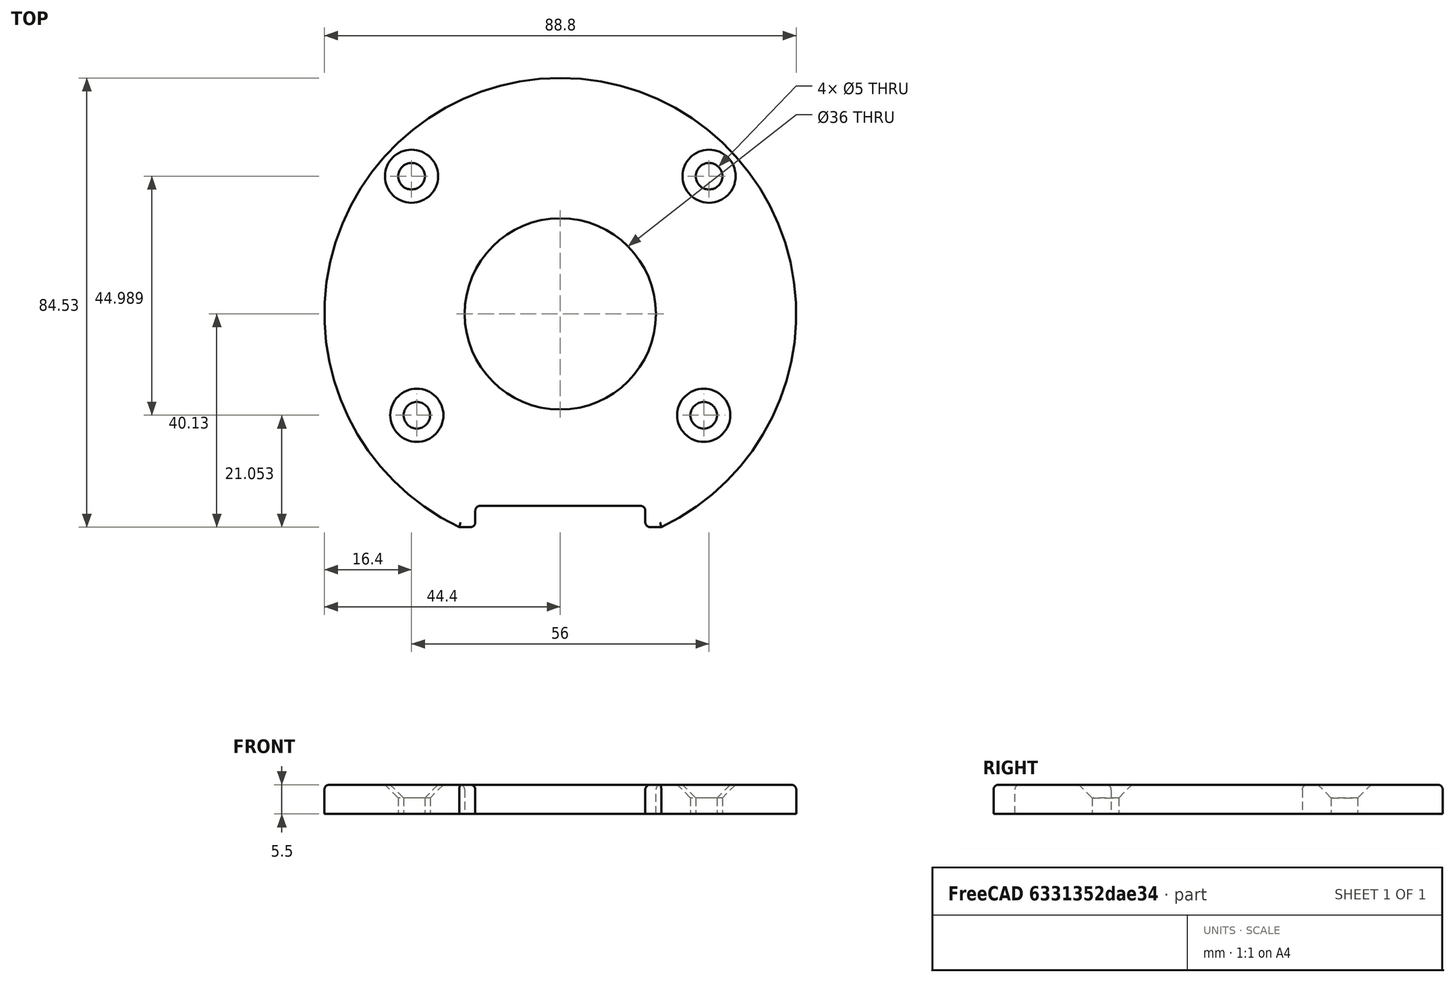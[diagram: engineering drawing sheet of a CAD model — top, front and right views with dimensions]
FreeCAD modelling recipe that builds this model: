
FCSTD DOCUMENT  (FreeCAD 0.19RUnknown)
Label: makita_RT0700CX4-2_base
License: All rights reserved
LicenseURL: http://en.wikipedia.org/wiki/All_rights_reserved
objects: Sketcher::SketchObject×2, PartDesign::Pad×1, PartDesign::Hole×1, PartDesign::Fillet×1, PartDesign::Body×1
note: 9 computed .brp shape members not serialized (recipe doc carries the construction recipe); baked Part::Feature solids carry a one-line shape summary decoded from their .brp

FEATURE [Sketcher::SketchObject] Sketch
  FullyConstrained = true
  MapMode = 5
  Support = -> [XY_Plane]
  sketch-geometry (7):
    g0: ArcOfCircle CenterX=0 CenterY=0 CenterZ=0 NormalX=0 NormalY=0 NormalZ=1 AngleXU=0 Radius=44.4 StartAngle=5.15459 EndAngle=10.5534
    g1: Circle CenterX=0 CenterY=0 CenterZ=0 NormalX=0 NormalY=0 NormalZ=1 AngleXU=0 Radius=18
    g2: LineSegment StartX=-19 StartY=-40.1293 StartZ=0 EndX=-16 EndY=-40.1293 EndZ=0
    g3: LineSegment StartX=-16 StartY=-40.1293 StartZ=0 EndX=-16 EndY=-36.1293 EndZ=0
    g4: LineSegment StartX=-16 StartY=-36.1293 StartZ=0 EndX=16 EndY=-36.1293 EndZ=0
    g5: LineSegment StartX=16 StartY=-36.1293 StartZ=0 EndX=16 EndY=-40.1293 EndZ=0
    g6: LineSegment StartX=16 StartY=-40.1293 StartZ=0 EndX=19 EndY=-40.1293 EndZ=0
  constraints (19):
    c: Coincident(g0,g-1)
    c: Diameter(g0) = 88.8
    c: Coincident(g1,g0)
    c: Diameter(g1) = 36
    c: Horizontal(g2)
    c: DistanceX(g2,g6) = 38
    c: Coincident(g0,g6)
    c: Coincident(g0,g2)
    c: Vertical(g3)
    c: Horizontal(g4)
    c: Vertical(g5)
    c: Coincident(g2,g3)
    c: Coincident(g6,g5)
    c: Tangent(g2,g6)
    c: Equal(g2,g6)
    c: DistanceY(g3,g3) = 4
    c: DistanceX(g2,g2) = 3
    c: Coincident(g3,g4)
    c: Coincident(g5,g4)
FEATURE [PartDesign::Pad] Pad
  Direction = (1,1,1)
  Length = 5.5
  Length2 = 100
  Profile = -> Sketch
  Type = 0
FEATURE [Sketcher::SketchObject] Sketch001
  ExternalGeometry = -> [Pad]
  FullyConstrained = true
  MapMode = 5
  Placement = pos=(0,0,5.5) rot=(0,0,1;0rad)
  Support = -> [Pad]
  sketch-geometry (5):
    g0: Circle CenterX=28 CenterY=25.9118 CenterZ=0 NormalX=0 NormalY=0 NormalZ=1 AngleXU=0 Radius=2.25
    g1: Circle CenterX=-28 CenterY=25.9118 CenterZ=0 NormalX=0 NormalY=0 NormalZ=1 AngleXU=0 Radius=2.25
    g2: LineSegment StartX=-32.5872 StartY=30.1569 StartZ=0 EndX=-28 EndY=25.9118 EndZ=0
    g3: Circle CenterX=-27 CenterY=-19.0771 CenterZ=0 NormalX=0 NormalY=0 NormalZ=1 AngleXU=0 Radius=2.25
    g4: Circle CenterX=27 CenterY=-19.0771 CenterZ=0 NormalX=0 NormalY=0 NormalZ=1 AngleXU=0 Radius=2.25
  constraints (13):
    c: Equal(g1,g0)
    c: Symmetric(g1,g0,g-2)
    c: Diameter(g0) = 4.5
    c: DistanceX(g1,g0) = 56
    c: PointOnObject(g2,g-3)
    c: Coincident(g2,g1)
    c: Perpendicular(g-3,g2)
    c: Distance(g2) = 6.25
    c: Equal(g3,g4)
    c: Equal(g0,g4)
    c: Symmetric(g3,g4,g-2)
    c: DistanceX(g3,g4) = 54
    c: Distance(g1,g3) = 45
FEATURE [PartDesign::Hole] Hole
  BaseFeature = -> Pad
  Depth = 25
  DepthType = 1
  Diameter = 5
  DrillPoint = 0
  DrillPointAngle = 118
  HoleCutCountersinkAngle = 90
  HoleCutDepth = 0
  HoleCutDiameter = 10
  HoleCutType = 2
  ModelActualThread = false
  Profile = -> Sketch001
  Tapered = false
  TaperedAngle = 90
  ThreadAngle = 60
  ThreadClass = 0
  ThreadCutOffInner = 0.0270633
  ThreadCutOffOuter = 0.0541266
  ThreadDirection = 0
  ThreadFit = 0
  ThreadPitch = 0.25
  ThreadSize = 12
  ThreadType = 1
  Threaded = false
FEATURE [PartDesign::Fillet] Fillet
  Base = -> Hole [Edge4,Edge24,Edge10,Edge20,Edge21,Edge19,Edge7,Edge8,Edge5,Edge28,Edge27]
  BaseFeature = -> Hole
  Radius = 0.9
  SupportTransform = false
FEATURE [PartDesign::Body] Body
  Group = -> [Sketch,Pad,Sketch001,Hole,Fillet]
  Origin = -> Origin
  Tip = -> Fillet
